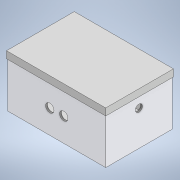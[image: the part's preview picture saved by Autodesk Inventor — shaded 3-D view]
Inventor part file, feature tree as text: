
AUTODESK INVENTOR PART (.ipt)
format: ipt  version: 2020 (Build 240168000, 168)  size: 184,832 bytes
history: native  units: mm
features: extrude x8, sketch x8, other x2, plane x2, projected_geometry x1
ambient origin geometry x8: Origin, YZ Plane, XZ Plane, XY Plane, X Axis, Y Axis, Z Axis, Center Point
bodies: Body1 (feature_tree)
feature tree (21):
  other  "Sólido1"
  extrude  "Extrusión1"  Depth=190.0mm
  other  "Eje de trabajo1"
  extrude  "Extrusión2"  Depth=140.0mm
  extrude  "Extrusión3"  Depth=270.0mm
  extrude  "Extrusión5"  Depth=180.0mm
  extrude  "Techo"  Depth=125.0mm TaperAngle=0.0deg
  extrude  "Extrusión7"  Depth=5.0mm TaperAngle=0.0deg
  extrude  "Extrusión8"  Depth=20.0mm
  extrude  "Extrusión10"  Depth=10.0mm TaperAngle=0.0deg
  sketch  "Boceto1"  dims[d0=280.0mm d1=190.0mm]
  plane  "Plano de trabajo1"
  plane  "Plano de trabajo2"
  sketch  "Boceto3"  dims[d2=95.0mm d3=140.0mm]
  projected_geometry  "Contorno proyectado1"
  sketch  "Boceto4"  dims[d4=130.0mm d5=0.0mm d7=270.0mm]
  sketch  "Boceto7"  dims[d8=135.0mm d9=180.0mm]
  sketch  "Boceto8"  dims[d10=90.0mm d11=125.0mm d12=0.0mm]
  sketch  "Boceto9"  dims[d13=20.0mm d14=5.0mm d15=0.0mm]
  sketch  "Boceto10"  dims[d18=20.0mm d19=68.0mm]
  sketch  "Boceto11"  dims[d20=140.0mm d21=10.0mm d22=0.0mm d23=2.0mm d24=2.0mm d25=2.0mm d26=2.0mm d27=20.0mm d28=0.0mm d29=24.0mm d30=24.0mm d31=68.0mm d32=40.0mm d34=10.0mm d35=0.0mm d36=20.3mm d37=95.0mm d38=30.0mm d39=10.0mm d40=0.0mm d45=9.0mm d46=60.0mm d47=95.0mm d48=10.0mm d49=0.0mm]
